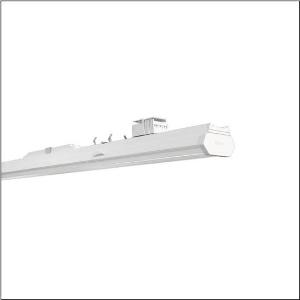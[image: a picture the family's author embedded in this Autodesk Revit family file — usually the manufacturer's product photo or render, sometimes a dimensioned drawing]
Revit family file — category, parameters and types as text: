
# Revit family: licross_r__21_protected_ho_52td11mn4fxs_06ba
name_source: partatom
category: Lighting Fixtures
units: mm (PartAtom-declared; Revit-internal decimal feet)

## family parameters
Cut with Voids When Loaded = No
Host = Face
Light Source = No
Part Type = Normal
Room Calculation Point = No
Round Connector Dimension = Use Diameter
Shared = No

## types (1)
- --- (1 x LED, 15020 lm, 83.2 W, 4000K)
    Apparent Load = 83 VA
    CIE Flux Codes = 84 94 98 99 100
    Color Rendering = 80
    Color Temperature = 4000K
    Default Elevation = 1800 mm
    Description = Licross® 21 Protected HO, luminaire insert, of sheet steel, galvanised, coil coated, white, length: 1.500mm, width: 66mm, height: 67mm, LED rated luminous flux: 15.020lm, light colour: 840, control gear: ON/OFF Multilumen, with plug, 3-pole, with phase selection, mains connection: 220..240V, AC, 50/60Hz, rated input power: 83W, halogen-free wiring, primary light control with lens, of plastic, primary optical cover: cover, of PMMA, light emission: direct distribution, primary light characteristic: symmetric, protection rating (complete): IP54, insulation class (complete): insulation class I (protective earthing), certification: CE, ENEC, VDE, UKCA, protection symbol: D if used in an environment with non-conductive dust loads with corresponding accessories, impact resistance: IK06, permissible ambient temperature for indoor applications: -35..+35°C, corresponds to IFS (International Featured Standards) requirements for safety and quality in the food industry, reducing of maximum allowable ambient temperature of 5°C with ceiling mounting, LABS conformity tested according to VDMA 24364:2018-05, packaging unit: 1 piece
    Height = 92 mm
    Lamp = 1 x LED
    Lamp Light Flux = 15020 lm
    Lamp Power = 83.2 W
    Lamp count = 1
    Length = 1500 mm
    Luminous efficacy = 181 lm/W
    Manufacturer = Siteco
    ModVariant = No
    Model = 52TD11MN4FXS
    Mounting Place = Ceiling
    Mounting Type = Pendant
    Number of Poles = 1
    OnlyDefault = Yes
    Power Factor = 1
    Product Name = Licross® 21 Protected HO
    Product group = luminaire insert
    ProductGroupID = 901
    Protection Class = Protection class I
    Protection Degree = IP 54
    RLX_Detail_Level = 1
    RLX_Emergency_Light_Flux = 0 lm
    RLX_Emergency_Type = 0
    RLX_Emergency_Type_DB = No
    RlxData = <blob elided: 21925 chars, md5=d62ca350>
    Socket = socket
    Standby Power = 0 W
    System Light Flux = 15020 lm
    System Power = 83 W
    Type Comments = factory setting: luminous flux: 100 % | (A | C | E) | 195 mA
    Type Image = l_1256148.jpg
    URL = http://relux.com
    VarID = @adj_057395
    Voltage = 0 V
    Weight = 0.00 kg
    Width = 88 mm

## geometry (parser evidence)
native form markers: Blend x4, Sweep x11
no freeform markers — native parametric forms only
